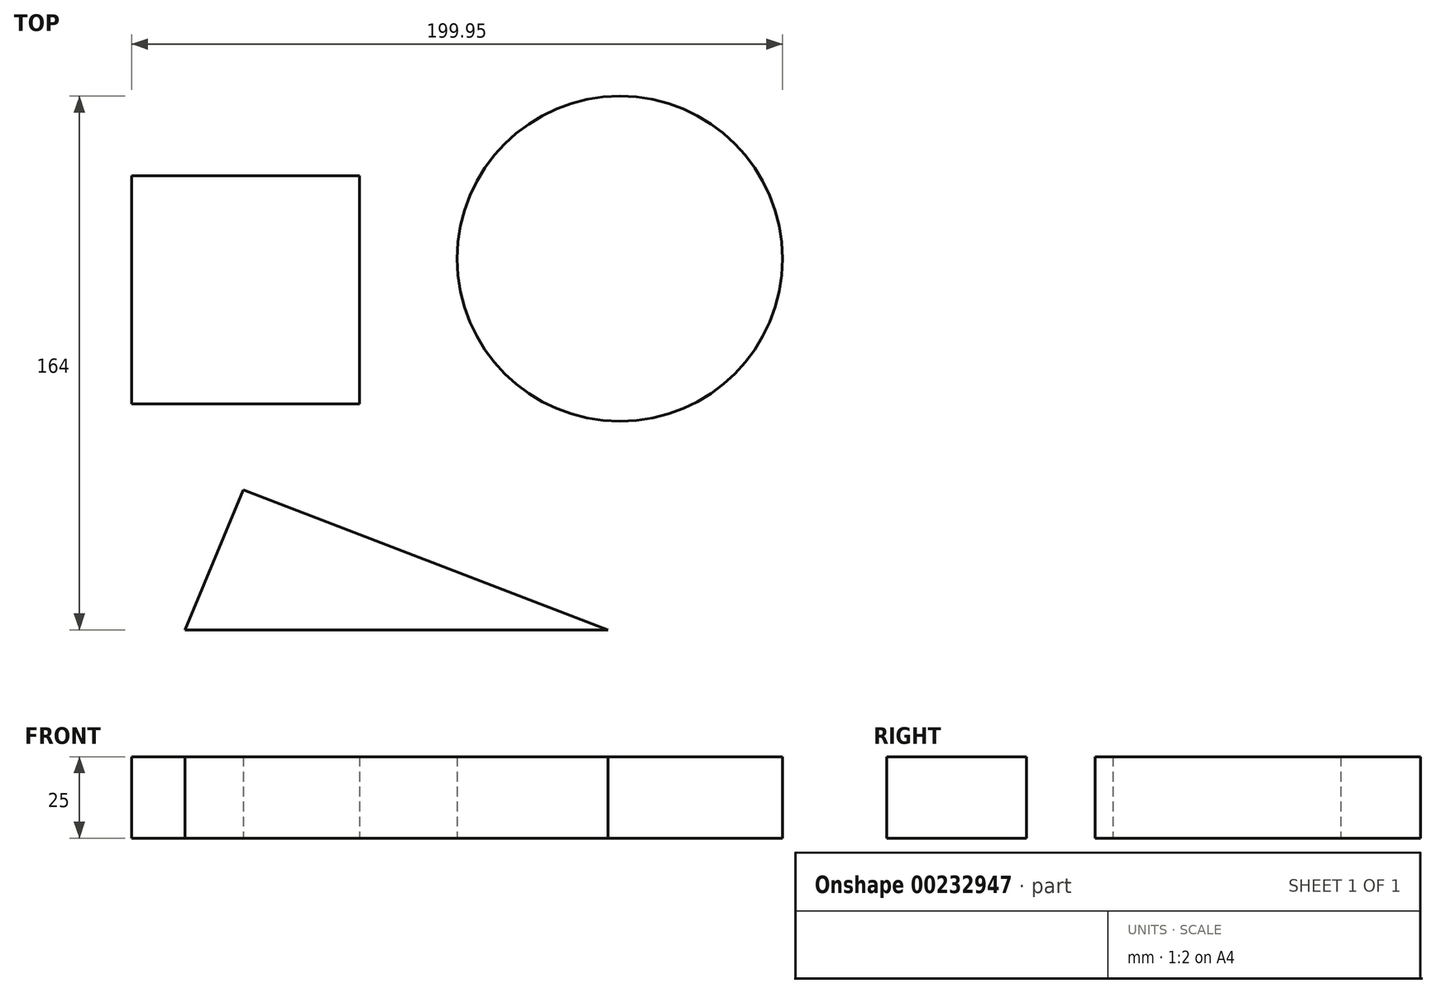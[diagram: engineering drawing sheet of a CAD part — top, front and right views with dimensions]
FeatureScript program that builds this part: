
annotation { "Feature Type Name" : "Feature", "Feature Type Description" : "" }
export const myFeature = defineFeature(function(context is Context, id is Id, definition is map)
    precondition{}
    {
        {
            var Q0;
            Q0=qCreatedBy(makeId("Top.planeOp"),FACE);
            var sketch = newSketch(context, id + "F0", { "sketchPlane" : qUnion([Q0])});
            skLineSegment(sketch, "E0", {"start": v(-72.89, 62.93) * mm, "end": v(-2.89, 62.93) * mm});
            skLineSegment(sketch, "E1", {"start": v(-72.89, 62.93) * mm, "end": v(-72.89, -7.07) * mm});
            skLineSegment(sketch, "E2", {"start": v(-72.89, -7.07) * mm, "end": v(-2.89, -7.07) * mm});
            skLineSegment(sketch, "E3", {"start": v(-2.89, 62.93) * mm, "end": v(-2.89, -7.07) * mm});
            skCircle(sketch, "E4", {"center": v(-37.89, 27.93) * mm, "radius": 34.72 * mm});
            skLineSegment(sketch, "E5.bottom", {"start": v(42.1, 72.48) * mm, "end": v(112.1, 72.48) * mm});
            skLineSegment(sketch, "E5.top", {"start": v(42.1, 2.48) * mm, "end": v(112.1, 2.48) * mm});
            skLineSegment(sketch, "E5.left", {"start": v(42.1, 72.48) * mm, "end": v(42.1, 2.48) * mm});
            skLineSegment(sketch, "E5.right", {"start": v(112.1, 72.48) * mm, "end": v(112.1, 2.48) * mm});
            skCircle(sketch, "E6", {"center": v(77.1, 37.48) * mm, "radius": 49.95 * mm});
            skLineSegment(sketch, "E7", {"start": v(-56.47, -76.56) * mm, "end": v(73.53, -76.56) * mm});
            skLineSegment(sketch, "E8", {"start": v(-56.47, -76.56) * mm, "end": v(-38.5, -33.56) * mm});
            skLineSegment(sketch, "E9", {"start": v(-38.5, -33.56) * mm, "end": v(73.53, -76.56) * mm});
            skCircle(sketch, "E10", {"center": v(-28.37, -57.38) * mm, "radius": 18.6 * mm});
            skPoint(sketch, "E10.first.point", {"position": v(-46.1, -51.73) * mm});
            skPoint(sketch, "E10.second.point", {"position": v(-10.73, -63.26) * mm});
            skPoint(sketch, "E10.third.point", {"position": v(-10.53, -52.14) * mm});
            skSolve(sketch);
        }
        {
            var Q0;
            Q0=makeQuery(id+"F0.imprint","IMPRINT",FACE,{"disambiguationData":[TD([[makeQuery(id+"F0.imprint","IMPRINT",EDGE,{"derivedFrom":sQuery(id+"F0.wireOp",EDGE,"E4")}),1.0]])]});
            var Q1;
            Q1=makeQuery(id+"F0.imprint","IMPRINT",FACE,{"disambiguationData":[TD([[makeQuery(id+"F0.imprint","IMPRINT",EDGE,{"derivedFrom":sQuery(id+"F0.wireOp",EDGE,"E0")}),-1.0]])]});
            var Q2;
            Q2=makeQuery(id+"F0.imprint","IMPRINT",FACE,{"disambiguationData":[TD([[makeQuery(id+"F0.imprint","IMPRINT",EDGE,{"derivedFrom":sQuery(id+"F0.wireOp",EDGE,"E5.bottom")}),-1.0]])]});
            var Q3;
            Q3=makeQuery(id+"F0.imprint","IMPRINT",FACE,{"disambiguationData":[TD([[makeQuery(id+"F0.imprint","IMPRINT",EDGE,{"derivedFrom":sQuery(id+"F0.wireOp",EDGE,"E5.bottom")}),1.0]])]});
            var Q4;
            {var subQ0=sQuery(id+"F0.wireOp",EDGE,"E10");var subQ1=sQuery(id+"F0.wireOp",EDGE,"E8");var subQ2=makeQuery(id+"F0.imprint","INTERSECT",VERTEX,{"disambiguationData":[OD(0.0)],"derivedFrom":[subQ1,subQ0]});Q4=makeQuery(id+"F0.imprint","IMPRINT",FACE,{"disambiguationData":[TD([[makeQuery(id+"F0.imprint","IMPRINT",EDGE,{"disambiguationData":[TD([[subQ2,-1.0]])],"derivedFrom":subQ1}),-1.0]])]});}
            var Q5;
            {var subQ4=sQuery(id+"F0.wireOp",EDGE,"E7");Q5=makeQuery(id+"F0.imprint","IMPRINT",FACE,{"disambiguationData":[TD([[makeQuery(id+"F0.imprint","IMPRINT",EDGE,{"derivedFrom":subQ4}),1.0]])]});}
            extrude(context, id + "F1", {"entities" : qUnion([Q0, Q1, Q2, Q3, Q4, Q5]), "depth" : 25 * mm});
        }
    });
